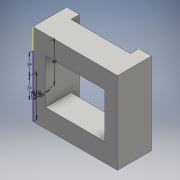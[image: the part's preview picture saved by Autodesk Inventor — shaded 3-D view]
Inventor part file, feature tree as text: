
AUTODESK INVENTOR PART (.ipt)
format: ipt  version: 2016 (Build 200138000, 138)  size: 130,048 bytes
history: native  units: mm
features: sketch x6, extrude x2, other x1
ambient origin geometry x8: Origin, YZ Plane, XZ Plane, XY Plane, X Axis, Y Axis, Z Axis, Center Point
bodies: Body1 (feature_tree), Body2 (feature_tree)
feature tree (9):
  other  "Bryła1"
  sketch  "Szkic1"
  sketch  "Szkic 3D1"
  sketch  "Szkic 3D2"
  extrude  "Wyciągnięcie proste1"  Depth=97.0mm
  sketch  "Szkic2"
  extrude  "Wyciągnięcie proste2"  Depth=70.0mm
  sketch  "Szkic4"
  sketch  "Szkic3"
